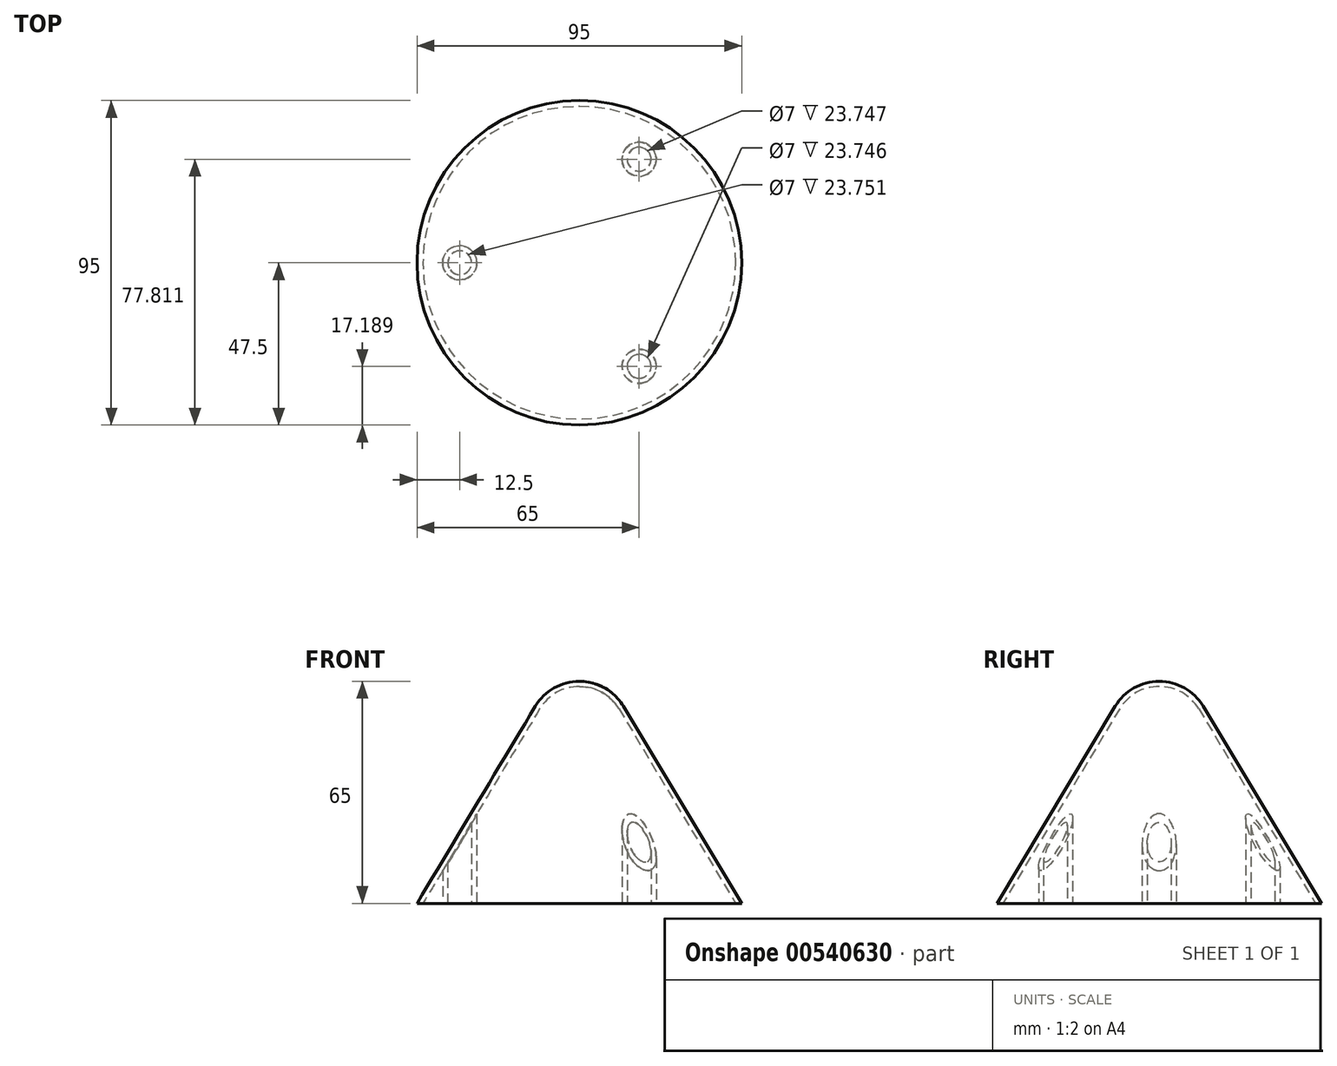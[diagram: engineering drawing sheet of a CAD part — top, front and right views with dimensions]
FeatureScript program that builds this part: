
annotation { "Feature Type Name" : "Feature", "Feature Type Description" : "" }
export const myFeature = defineFeature(function(context is Context, id is Id, definition is map)
    precondition{}
    {
        {
            var Q0;
            Q0=qCreatedBy(makeId("Front.planeOp"),FACE);
            var sketch = newSketch(context, id + "F0", { "sketchPlane" : qUnion([Q0])});
            skLineSegment(sketch, "E0", {"start": v(0, 0) * mm, "end": v(47.5, 0) * mm});
            skLineSegment(sketch, "E1", {"start": v(0, 0) * mm, "end": v(0, 50) * mm});
            skArc(sketch, "E2", {"start": v(12.86, 57.72) * mm, "mid": v(7.39, 63.05) * mm, "end": v(0, 65) * mm});
            skLineSegment(sketch, "E3", {"start": v(12.86, 57.72) * mm, "end": v(47.5, 0) * mm});
            skLineSegment(sketch, "E4", {"start": v(0, 0) * mm, "end": v(0, 65) * mm});
            skPoint(sketch, "E5.orphan", {"position": v(-12.86, 57.72) * mm});
            skSolve(sketch);
        }
        {
            var Q0;
            {var subQ0=sQuery(id+"F0.wireOp",EDGE,"E0");Q0=makeQuery(id+"F0.imprint","IMPRINT",FACE,{"disambiguationData":[TD([[makeQuery(id+"F0.imprint","IMPRINT",EDGE,{"derivedFrom":subQ0}),1.0]])]});}
            var Q1;
            Q1=sQuery(id+"F0.wireOp",EDGE,"E4");
            revolve(context, id + "F1", {"entities" : qUnion([Q0]), "axis" : qUnion([Q1]), "revolveType" : RevolveType.FULL});
        }
        {
            var Q0;
            Q0=makeQuery(id+"F1.opRevolve","SWEPT_FACE",FACE,{"disambiguationData":[OSD([sQuery(id+"F0.wireOp",EDGE,"E0")])]});
            shell(context, id + "F2", {"entities" : qUnion([Q0]), "thickness" : 1.5 * mm});
        }
        {
            var Q0;
            Q0=qCreatedBy(makeId("Top.planeOp"),FACE);
            var sketch = newSketch(context, id + "F3", { "sketchPlane" : qUnion([Q0])});
            skCircle(sketch, "E6", {"center": v(-35, 0) * mm, "radius": 5 * mm});
            skCircle(sketch, "E7.1.0", {"center": v(17.5, -30.31) * mm, "radius": 5 * mm});
            skCircle(sketch, "E7.2.0", {"center": v(17.5, 30.31) * mm, "radius": 5 * mm});
            skPoint(sketch, "E7.center", {"position": v(0, 0) * mm});
            skSolve(sketch);
        }
        {
            var Q0;
            Q0 = qSketchRegion(id + "F3", true);
            extrude(context, id + "F4", {"entities" : qUnion([Q0]), "operationType" : NewBodyOperationType.ADD, "endBound" : BoundingType.UP_TO_NEXT, "depth" : 25 * mm, "offsetDistance" : 25 * mm});
        }
        {
            var Q0;
            Q0=makeQuery(id+"F4.opExtrude","CAP_FACE",FACE,{"disambiguationData":[OSD([sQuery(id+"F3.wireOp",EDGE,"E7.1.0")])],"isStart":true});
            var Q1;
            Q1=makeQuery(id+"F4.opExtrude","CAP_FACE",FACE,{"disambiguationData":[OSD([sQuery(id+"F3.wireOp",EDGE,"E7.2.0")])],"isStart":true});
            var Q2;
            Q2=makeQuery(id+"F4.opExtrude","CAP_FACE",FACE,{"disambiguationData":[OSD([sQuery(id+"F3.wireOp",EDGE,"E6")])],"isStart":true});
            shell(context, id + "F5", {"entities" : qUnion([Q0, Q1, Q2]), "thickness" : 1.5 * mm});
        }
    });
